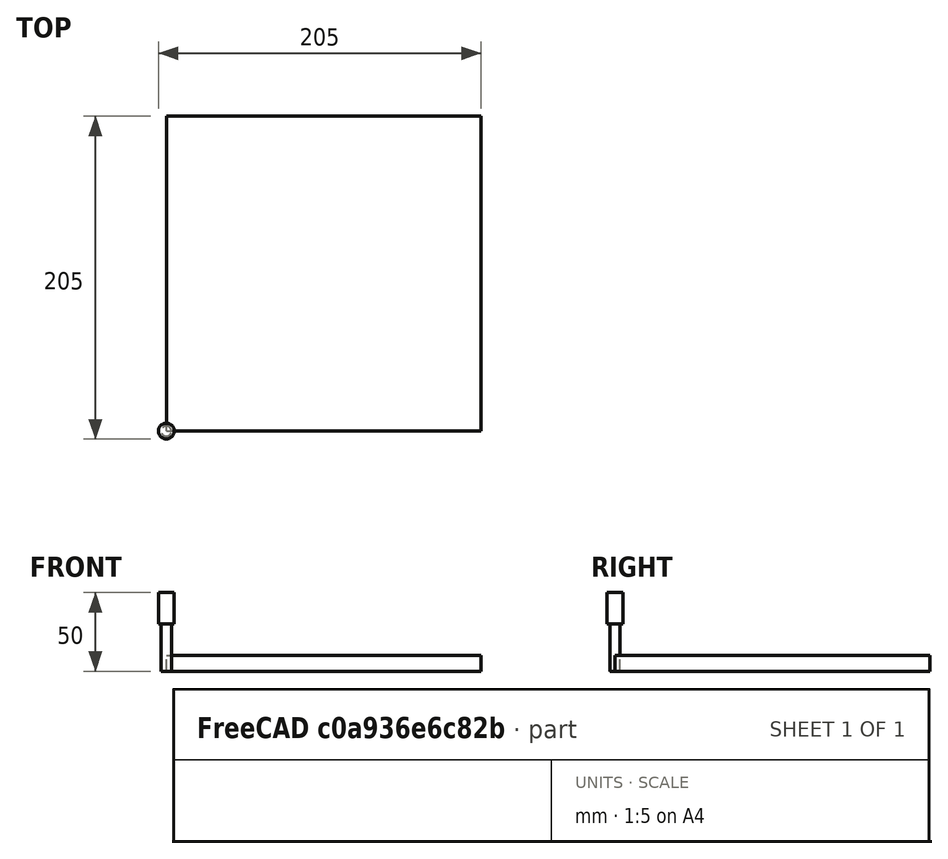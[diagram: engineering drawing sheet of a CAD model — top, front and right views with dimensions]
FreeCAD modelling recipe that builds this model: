
FCSTD DOCUMENT  (FreeCAD 0.20RUnknown)
Label: 2doffset
License: All rights reserved
LicenseURL: http://en.wikipedia.org/wiki/All_rights_reserved
objects: Part::FeaturePython×4, App::DocumentObjectGroup×3, Path::FeaturePython×3, Sketcher::SketchObject×2, Mesh::FeaturePython×2, PartDesign::Pad×1, PartDesign::Body×1, Part::Offset2D×1, App::FeaturePython×1
note: 11 computed .brp shape members not serialized (recipe doc carries the construction recipe); baked Part::Feature solids carry a one-line shape summary decoded from their .brp

FEATURE [Sketcher::SketchObject] Sketch
  FullyConstrained = true
  MapMode = 5
  Support = -> [XY_Plane]
  sketch-geometry (4):
    g0: LineSegment StartX=0 StartY=200 StartZ=0 EndX=200 EndY=200 EndZ=0
    g1: LineSegment StartX=200 StartY=200 StartZ=0 EndX=200 EndY=0 EndZ=0
    g2: LineSegment StartX=200 StartY=0 StartZ=0 EndX=0 EndY=0 EndZ=0
    g3: LineSegment StartX=0 StartY=0 StartZ=0 EndX=0 EndY=200 EndZ=0
  constraints (11):
    c: Coincident(g0,g1)
    c: Coincident(g1,g2)
    c: Coincident(g2,g3)
    c: Coincident(g3,g0)
    c: Horizontal(g0)
    c: Horizontal(g2)
    c: Vertical(g1)
    c: Vertical(g3)
    c: Coincident(g2,g-1)
    c: DistanceY(g3,g3) = 200
    c: DistanceX(g2,g2) = 200
FEATURE [PartDesign::Pad] Pad
  Direction = (0,0,1)
  Length = 10
  Length2 = 10
  Profile = -> Sketch
  ReferenceAxis = -> Sketch [N_Axis]
  Type = 0
FEATURE [Sketcher::SketchObject] Sketch001
  FullyConstrained = false
  MapMode = 5
  Placement = pos=(0,0,10) rot=(0,0,1;0rad)
  Support = -> [Pad]
  sketch-geometry (14):
    g0: LineSegment StartX=24.7906 StartY=128.962 StartZ=0 EndX=24.7906 EndY=165.232 EndZ=0
    g1: ArcOfCircle CenterX=39.7906 CenterY=165.232 CenterZ=0 NormalX=0 NormalY=0 NormalZ=1 AngleXU=0 Radius=15 StartAngle=1.40022 EndAngle=3.14159
    g2: LineSegment StartX=42.3368 StartY=180.015 StartZ=0 EndX=156.884 EndY=160.284 EndZ=0
    g3: ArcOfCircle CenterX=154.338 CenterY=145.502 CenterZ=0 NormalX=0 NormalY=0 NormalZ=1 AngleXU=0 Radius=15 StartAngle=4.86359 EndAngle=7.68341
    g4: LineSegment StartX=156.598 StartY=130.673 StartZ=0 EndX=74.8549 EndY=118.218 EndZ=0
    g5: ArcOfCircle CenterX=77.1143 CenterY=103.389 CenterZ=0 NormalX=0 NormalY=0 NormalZ=1 AngleXU=0 Radius=15 StartAngle=1.722 EndAngle=4.65454
    g6: LineSegment StartX=76.2469 StartY=88.4143 StartZ=0 EndX=159.557 EndY=83.5891 EndZ=0
    g7: ArcOfCircle CenterX=158.689 CenterY=68.6142 CenterZ=0 NormalX=0 NormalY=0 NormalZ=1 AngleXU=0 Radius=15 StartAngle=4.87271 EndAngle=7.79613
    g8: LineSegment StartX=161.084 StartY=53.8066 StartZ=0 EndX=154.694 EndY=52.7732 EndZ=0
    g9: LineSegment StartX=24.7906 StartY=114.196 StartZ=0 EndX=24.7906 EndY=49.3875 EndZ=0
    g10: ArcOfCircle CenterX=39.7906 CenterY=49.3875 CenterZ=0 NormalX=0 NormalY=0 NormalZ=1 AngleXU=0 Radius=15 StartAngle=3.14159 EndAngle=4.87271
    g11: LineSegment StartX=42.1851 StartY=34.5799 StartZ=0 EndX=143.496 EndY=50.9625 EndZ=0
    g12: LineSegment StartX=42.1851 StartY=34.5799 StartZ=0 EndX=161.084 EndY=53.8066 EndZ=0
    g13: LineSegment StartX=24.7906 StartY=165.232 StartZ=0 EndX=24.7906 EndY=49.3875 EndZ=0
  constraints (24):
    c: Vertical(g0)
    c: Tangent(g0,g1) = 1.5708
    c: Tangent(g1,g2) = 1.5708
    c: Tangent(g2,g3) = 1.5708
    c: Tangent(g3,g4) = 1.5708
    c: Tangent(g4,g5) = -1.5708
    c: Tangent(g5,g6) = -1.5708
    c: Tangent(g6,g7) = 1.5708
    c: Tangent(g7,g8) = 1.5708
    c: Vertical(g9)
    c: Tangent(g9,g10) = -1.5708
    c: Tangent(g10,g11) = -1.5708
    c: Coincident(g12,g10)
    c: Coincident(g12,g7)
    c: Coincident(g13,g0)
    c: Coincident(g13,g9)
    c: Vertical(g13)
    c: PointOnObject(g11,g12)
    c: PointOnObject(g8,g12)
    c: Radius(g1) = 15
    c: Equal(g1,g10)
    c: Equal(g10,g7)
    c: Equal(g7,g5)
    c: Equal(g5,g3)
FEATURE [PartDesign::Body] Body
  Group = -> [Sketch,Pad,Sketch001]
  Origin = -> Origin
  Tip = -> Pad
FEATURE [Part::Offset2D] Offset2D
  Fill = false
  Intersection = false
  Join = 0
  Mode = 1
  SelfIntersection = false
  Source = -> Sketch001
  Value = 5
FEATURE [App::FeaturePython] SetupSheet  # Path/CAM operation (typed FeaturePython)
  ClearanceHeightExpression = OpStockZMax+SetupSheet.ClearanceHeightOffset
  ClearanceHeightOffset = 5
  CoolantMode = 0
  CoolantModes = None | Flood | Mist
  FinalDepthExpression = OpFinalDepth
  HorizRapid = 0
  SafeHeightExpression = OpStockZMax+SetupSheet.SafeHeightOffset
  SafeHeightOffset = 3
  StartDepthExpression = OpStartDepth
  StepDownExpression = OpToolDiameter
  VertRapid = 0
FEATURE [Part::FeaturePython] Clone  label="Model-Body"  # Draft clone (typed FeaturePython)
  AttacherType = Attacher::AttachEngine3D
  Fuse = false
  Objects = -> [Body]
  PathResource = Model
  Scale = (1,1,1)
FEATURE [Part::FeaturePython] Clone001  label="Model-Offset2D"  # Draft clone (typed FeaturePython)
  AttacherType = Attacher::AttachEngine3D
  Fuse = false
  Objects = -> [Offset2D]
  PathResource = Model
  Scale = (1,1,1)
FEATURE [App::DocumentObjectGroup] Model
  Group = -> [Clone,Clone001]
FEATURE [Part::FeaturePython] Stock  # WARN: FeaturePython — macro-defined, semantics opaque (R4)
  Height = 10
  Length = 200
  StockType = CreateBox
  Width = 200
FEATURE [Part::FeaturePython] ToolBit001  label="6.4mm Endmill"  # Path/CAM toolbit (typed FeaturePython)
  BitPropertyNames = Chipload | CuttingEdgeHeight | Diameter | Flutes | Length | Material | ShankDiameter | SpindleDirection
  BitShape = <path>
  Chipload = 0
  CuttingEdgeHeight = 30
  Diameter = 6.4
  File = <userpath>/Documents/Sherline/FreeCAD/Bit/6.4mm_Endmill.fctb
  Flutes = 0
  Length = 50
  Material = 0
  ShankDiameter = 10
  ShapeName = endmill
  SpindleDirection = 0
FEATURE [Path::FeaturePython] __4mm_Endmill  label="6.4mm Endmill001"  # Path/CAM operation (typed FeaturePython)
  HorizFeed = 15
  HorizRapid = 0
  SpindleDir = 0
  SpindleSpeed = 12000
  Tool = -> ToolBit001
  ToolNumber = 2
  VertFeed = 3.33333
  VertRapid = 0
  expr: HorizRapid = SetupSheet.HorizRapid
  expr: VertRapid = SetupSheet.VertRapid
FEATURE [App::DocumentObjectGroup] Tools
  Group = -> [__4mm_Endmill]
FEATURE [Path::FeaturePython] Profile  # Path/CAM operation (typed FeaturePython)
  Active = true
  AreaParams:
    Tolerance = 1e-07
    FitArcs = True
    Simplify = False
    CleanDistance = 0.0
    Accuracy = 0.01
    Unit = 1.0
    MinArcPoints = 4
    MaxArcPoints = 100
    ClipperScale = 10000000.0
    Fill = 0
    Coplanar = 0
    Reorient = True
    Outline = False
    Explode = False
    OpenMode = 0
    Deflection = 0.01
    SubjectFill = 0
    ClipFill = 0
    Offset = -3.2
    ExtraPass = 0
    Stepover = 0.0
    LastStepover = 0.0
    JoinType = 0
    EndType = 0
    MiterLimit = 2.0
    RoundPrecision = 0.0
    PocketMode = 0
    ToolRadius = 1.0
    PocketExtraOffset = 0.0
    PocketStepover = 0.0
    PocketLastStepover = 0.0
    FromCenter = False
    Angle = 45.0
    AngleShift = 0.0
    Shift = 0.0
    Thicken = False
    SectionCount = -1
    Stepdown = 1.0
    SectionOffset = 0.0
    SectionTolerance = 1e-06
    SectionMode = 2
    Project = False
  Base = -> [Clone001]
  ClearanceHeight = 15
  CoolantMode = 0
  CycleTime = 00:04:36
  Direction = 0
  FinalDepth = 0
  HandleMultipleFeatures = 0
  JoinType = 0
  MiterLimit = 0.1
  OffsetExtra = 0
  OpFinalDepth = 10
  OpStartDepth = 14
  OpStockZMax = 10
  OpStockZMin = 0
  OpToolDiameter = 6.4
  PathParams = {'orientation': 1, 'feedrate': 15.0, 'feedrate_v': 3.3333333333333335, 'verbose': True, 'resume_height': 13.0, 'retraction': 15.0, 'return_end': True, 'preamble': False, 'start': Vector (143.54177817028028, 52.75538036327148, 15.0)}
  SafeHeight = 13
  Side = 1
  SplitArcs = false
  StartDepth = 10
  StartPoint = (0,0,0)
  StepDown = 4
  ToolController = -> __4mm_Endmill
  UseComp = true
  UseStartPoint = false
  processCircles = false
  processHoles = false
  processPerimeter = true
  expr: ClearanceHeight = OpStockZMax + SetupSheet.ClearanceHeightOffset
  expr: FinalDepth = 0
  expr: SafeHeight = OpStockZMax + SetupSheet.SafeHeightOffset
  expr: StartDepth = 10
  expr: StepDown = 4
FEATURE [App::DocumentObjectGroup] Operations
  Group = -> [Profile]
FEATURE [Path::FeaturePython] Job  # Path/CAM operation (typed FeaturePython)
  CycleTime = 00:04:36
  Fixtures = G54
  GeometryTolerance = 0.01
  JobType = 0
  Model = -> Model
  Operations = -> Operations
  OrderOutputBy = 0
  PostProcessor = 2
  PostProcessorOutputFile = %D/%d.ngc
  SetupSheet = -> SetupSheet
  SplitOutput = false
  Stock = -> Stock
  Tools = -> Tools
FEATURE [Mesh::FeaturePython] CutMaterial  # WARN: FeaturePython — macro-defined, semantics opaque (R4)
FEATURE [Mesh::FeaturePython] CutMaterial001  # WARN: FeaturePython — macro-defined, semantics opaque (R4)
note: 1 file-system path scrubbed to <path> (originals preserved in the JSON sidecar)
